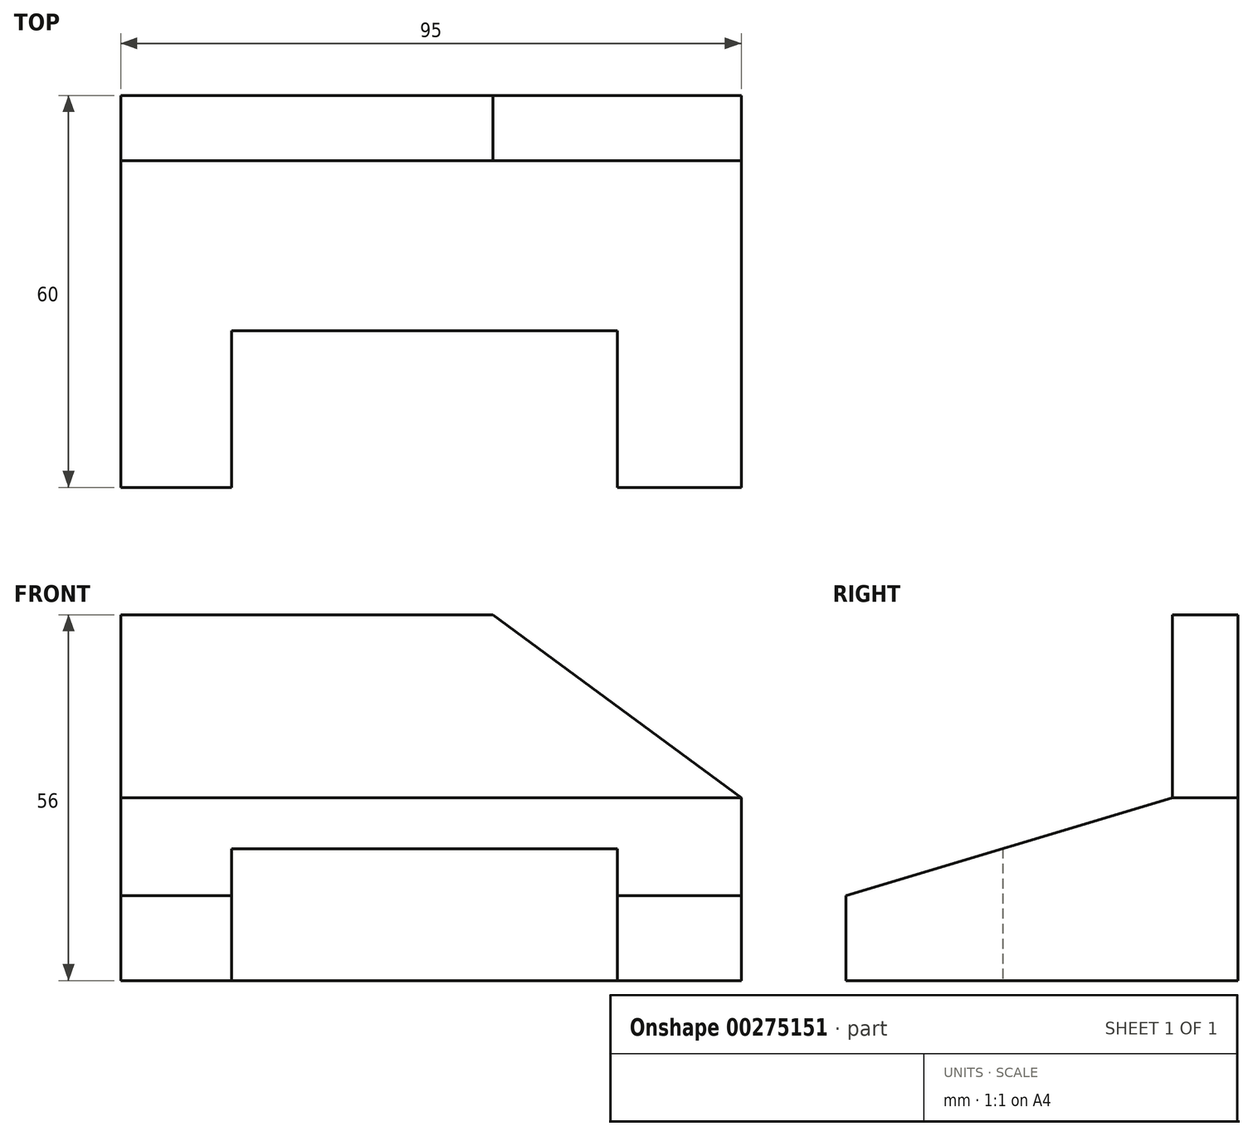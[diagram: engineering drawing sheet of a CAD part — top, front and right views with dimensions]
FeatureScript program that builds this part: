
annotation { "Feature Type Name" : "Feature", "Feature Type Description" : "" }
export const myFeature = defineFeature(function(context is Context, id is Id, definition is map)
    precondition{}
    {
        {
            var Q0;
            Q0=qCreatedBy(makeId("Right.planeOp"),FACE);
            var sketch = newSketch(context, id + "F0", { "sketchPlane" : qUnion([Q0])});
            skLineSegment(sketch, "E0", {"start": v(0.03, -0.45) * mm, "end": v(0.03, 55.55) * mm});
            skLineSegment(sketch, "E1", {"start": v(0.03, 55.55) * mm, "end": v(-9.97, 55.55) * mm});
            skLineSegment(sketch, "E2", {"start": v(-9.97, 55.55) * mm, "end": v(-9.97, 27.55) * mm});
            skLineSegment(sketch, "E3", {"start": v(-9.97, 27.55) * mm, "end": v(-59.97, 12.55) * mm});
            skLineSegment(sketch, "E4", {"start": v(-59.97, 12.55) * mm, "end": v(-59.97, -0.45) * mm});
            skLineSegment(sketch, "E5", {"start": v(-59.97, -0.45) * mm, "end": v(0.03, -0.45) * mm});
            skSolve(sketch);
        }
        {
            var Q0;
            Q0 = qSketchRegion(id + "F0", true);
            extrude(context, id + "F1", {"entities" : qUnion([Q0]), "depth" : 95 * mm});
        }
        {
            var Q0;
            Q0=makeQuery(id+"F1.opExtrude","SWEPT_FACE",FACE,{"disambiguationData":[OSD([sQuery(id+"F0.wireOp",EDGE,"E2")])]});
            var sketch = newSketch(context, id + "F2", { "sketchPlane" : qUnion([Q0])});
            skLineSegment(sketch, "E6", {"start": v(57, 55.55) * mm, "end": v(95, 27.55) * mm});
            skSolve(sketch);
        }
        {
            var Q0;
            {var subQ0=sQuery(id+"F2.wireOp",EDGE,"E6");Q0=makeQuery(id+"F2.imprint","IMPRINT",FACE,{"disambiguationData":[TD([[makeQuery(id+"F2.imprint","IMPRINT",EDGE,{"derivedFrom":subQ0}),1.0]])]});}
            extrude(context, id + "F3", {"entities" : qUnion([Q0]), "operationType" : NewBodyOperationType.REMOVE, "endBound" : BoundingType.THROUGH_ALL, "oppositeDirection" : true, "depth" : 25 * mm});
        }
        {
            var Q0;
            Q0=makeQuery(id+"F1.opExtrude","SWEPT_FACE",FACE,{"disambiguationData":[OSD([sQuery(id+"F0.wireOp",EDGE,"E5")])]});
            var sketch = newSketch(context, id + "F4", { "sketchPlane" : qUnion([Q0])});
            skLineSegment(sketch, "E7.bottom", {"start": v(17, 59.97) * mm, "end": v(76, 59.97) * mm});
            skLineSegment(sketch, "E7.top", {"start": v(17, 35.97) * mm, "end": v(76, 35.97) * mm});
            skLineSegment(sketch, "E7.left", {"start": v(17, 59.97) * mm, "end": v(17, 35.97) * mm});
            skLineSegment(sketch, "E7.right", {"start": v(76, 59.97) * mm, "end": v(76, 35.97) * mm});
            skSolve(sketch);
        }
        {
            var Q0;
            Q0 = qSketchRegion(id + "F4", true);
            extrude(context, id + "F5", {"entities" : qUnion([Q0]), "operationType" : NewBodyOperationType.REMOVE, "endBound" : BoundingType.THROUGH_ALL, "oppositeDirection" : true, "depth" : 25 * mm});
        }
    });
